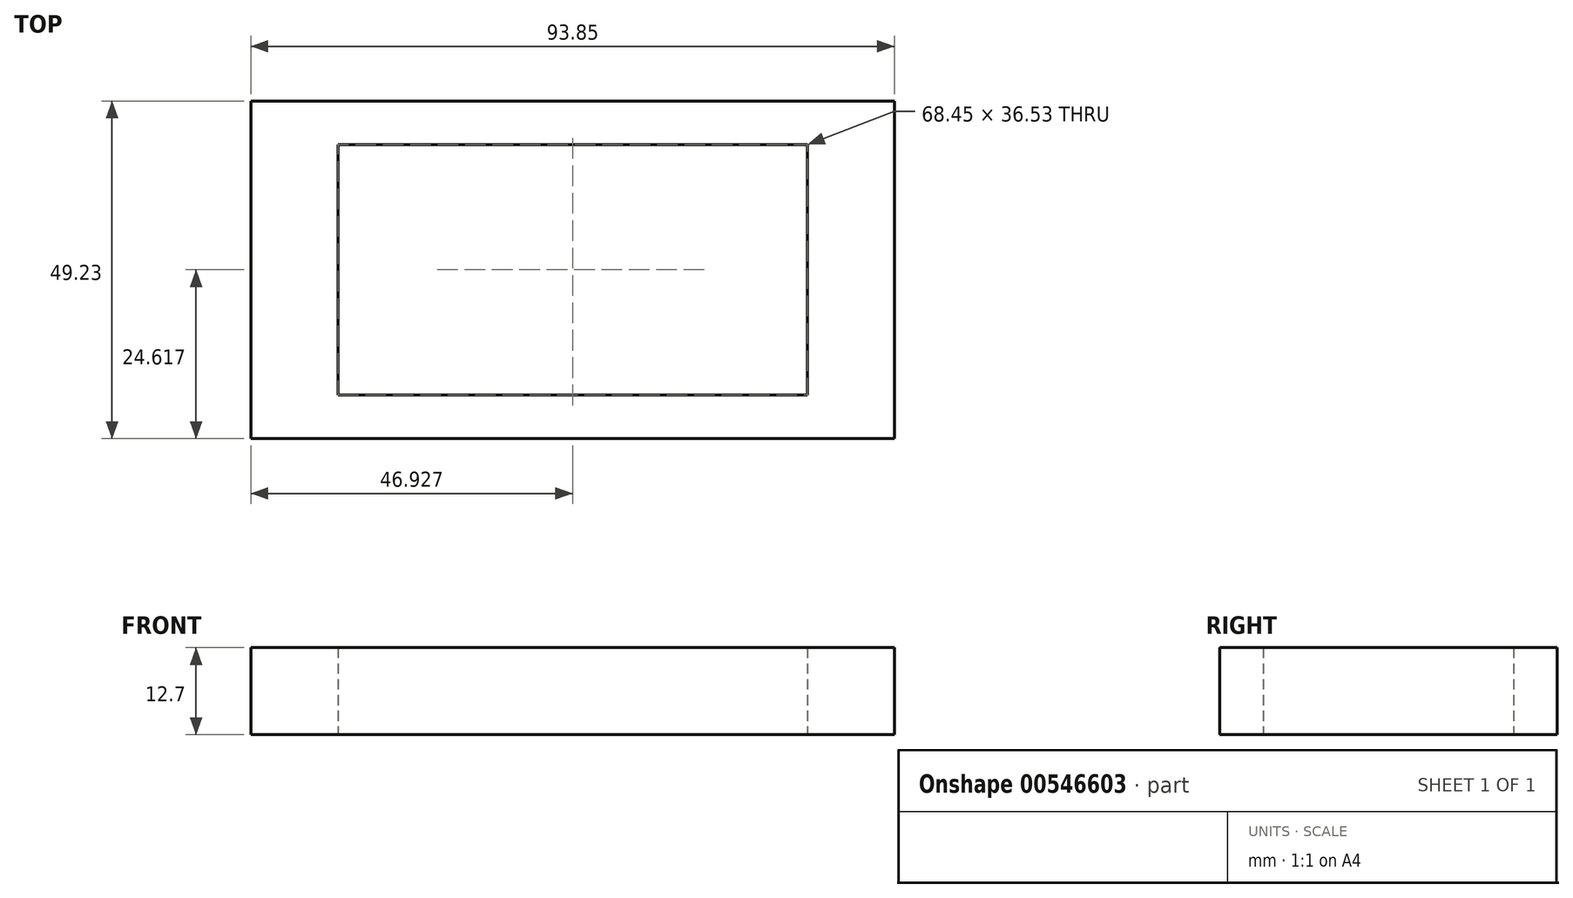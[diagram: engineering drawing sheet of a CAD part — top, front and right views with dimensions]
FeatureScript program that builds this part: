
annotation { "Feature Type Name" : "Feature", "Feature Type Description" : "" }
export const myFeature = defineFeature(function(context is Context, id is Id, definition is map)
    precondition{}
    {
        {
            var Q0;
            Q0=qCreatedBy(makeId("Top.planeOp"),FACE);
            var sketch = newSketch(context, id + "F0", { "sketchPlane" : qUnion([Q0])});
            skLineSegment(sketch, "E0.bottom", {"start": v(-12.7, 6.35) * mm, "end": v(81.15, 6.35) * mm});
            skLineSegment(sketch, "E0.top", {"start": v(-12.7, -42.88) * mm, "end": v(81.15, -42.88) * mm});
            skLineSegment(sketch, "E0.left", {"start": v(-12.7, 6.35) * mm, "end": v(-12.7, -42.88) * mm});
            skLineSegment(sketch, "E0.right", {"start": v(81.15, 6.35) * mm, "end": v(81.15, -42.88) * mm});
            skLineSegment(sketch, "E1.bottom", {"start": v(0, 0) * mm, "end": v(68.45, 0) * mm});
            skLineSegment(sketch, "E1.top", {"start": v(0, -36.53) * mm, "end": v(68.45, -36.53) * mm});
            skLineSegment(sketch, "E1.left", {"start": v(0, 0) * mm, "end": v(0, -36.53) * mm});
            skLineSegment(sketch, "E1.right", {"start": v(68.45, 0) * mm, "end": v(68.45, -36.53) * mm});
            skSolve(sketch);
        }
        {
            var Q0;
            Q0=qSketchRegion(id+"F0",true);
            extrude(context, id + "F1", {"entities" : qUnion([Q0]), "depth" : 12.7 * mm});
        }
    });
